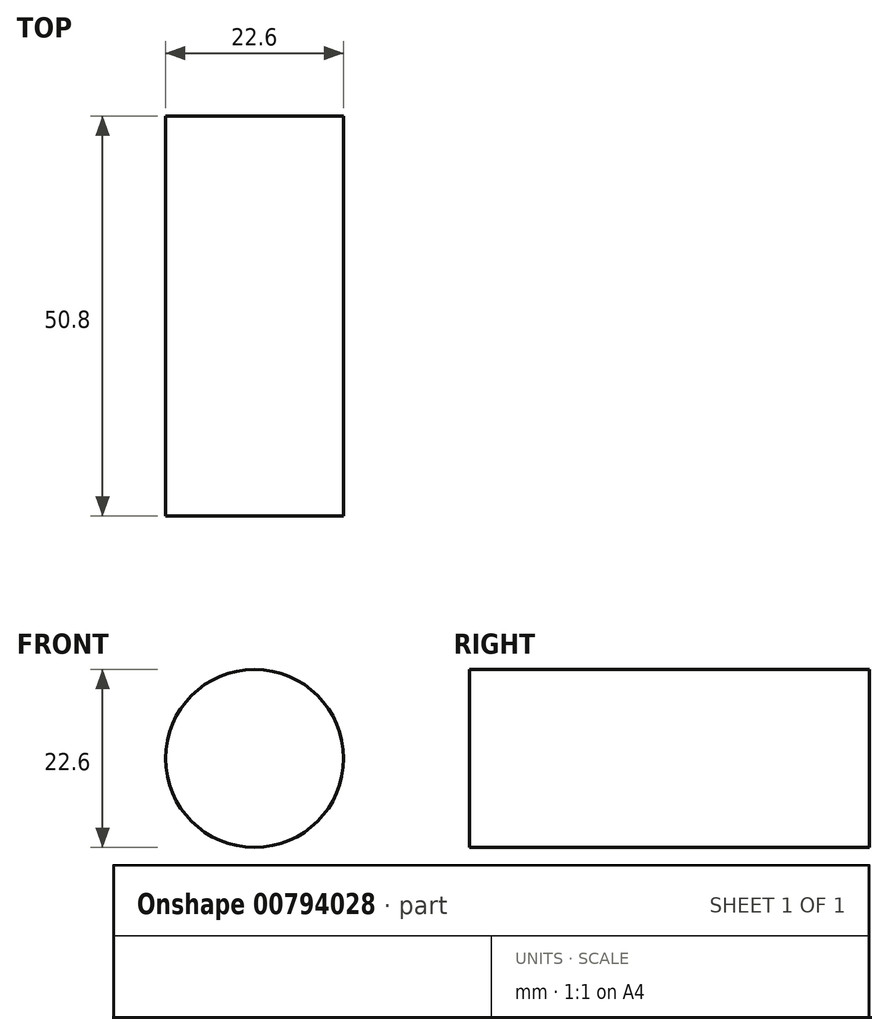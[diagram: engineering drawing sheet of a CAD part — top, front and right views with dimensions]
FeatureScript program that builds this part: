
annotation { "Feature Type Name" : "Feature", "Feature Type Description" : "" }
export const myFeature = defineFeature(function(context is Context, id is Id, definition is map)
    precondition{}
    {
        {
            var Q0;
            Q0=qCreatedBy(makeId("Front.planeOp"),FACE);
            var sketch = newSketch(context, id + "F0", { "sketchPlane" : qUnion([Q0])});
            skCircle(sketch, "E0", {"center": v(-61.23, 61.23) * mm, "radius": 11.3 * mm});
            skSolve(sketch);
        }
        {
            var Q0;
            Q0=makeQuery(id+"F0.imprint","IMPRINT",FACE,{"disambiguationData":[TD([[makeQuery(id+"F0.imprint","IMPRINT",EDGE,{"derivedFrom":sQuery(id+"F0.wireOp",EDGE,"E0")}),1.0]])]});
            extrude(context, id + "F1", {"entities" : qUnion([Q0]), "depth" : 50.8 * mm, "offsetDistance" : 25.4 * mm});
        }
    });
